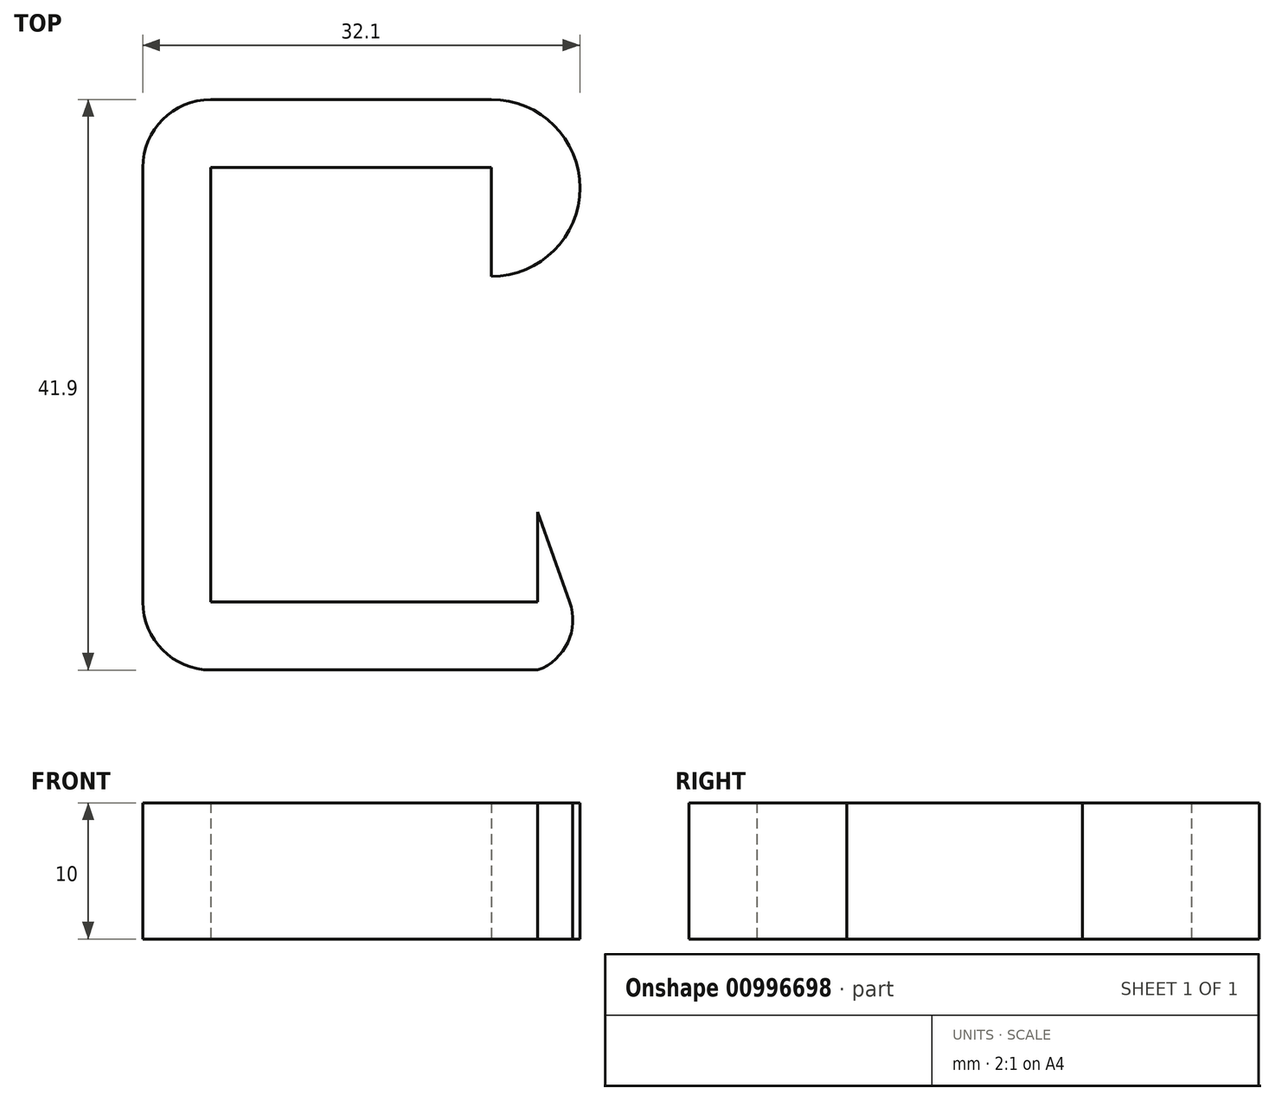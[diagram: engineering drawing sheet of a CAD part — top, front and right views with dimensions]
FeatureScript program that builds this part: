
annotation { "Feature Type Name" : "Feature", "Feature Type Description" : "" }
export const myFeature = defineFeature(function(context is Context, id is Id, definition is map)
    precondition{}
    {
        {
            var Q0;
            Q0=qCreatedBy(makeId("Top.planeOp"),FACE);
            var sketch = newSketch(context, id + "F0", { "sketchPlane" : qUnion([Q0])});
            skLineSegment(sketch, "E0", {"start": v(4.2, 20.2) * mm, "end": v(-16.4, 20.2) * mm});
            skLineSegment(sketch, "E1", {"start": v(-16.4, 20.2) * mm, "end": v(-16.4, -11.7) * mm});
            skLineSegment(sketch, "E2", {"start": v(-16.4, -11.7) * mm, "end": v(7.6, -11.7) * mm});
            skLineSegment(sketch, "E3", {"start": v(4.2, 20.2) * mm, "end": v(4.2, 12.2) * mm});
            skLineSegment(sketch, "E4.0", {"start": v(4.2, 25.2) * mm, "end": v(-16.4, 25.2) * mm});
            skLineSegment(sketch, "E5.0", {"start": v(-21.4, 20.2) * mm, "end": v(-21.4, -11.7) * mm});
            skLineSegment(sketch, "E6.0", {"start": v(-16.4, -16.7) * mm, "end": v(7.6, -16.7) * mm});
            skArc(sketch, "E7", {"start": v(-21.4, -11.7) * mm, "mid": v(-19.94, -15.24) * mm, "end": v(-16.4, -16.7) * mm});
            skArc(sketch, "E8", {"start": v(-16.4, 25.2) * mm, "mid": v(-19.94, 23.73) * mm, "end": v(-21.4, 20.2) * mm});
            skArc(sketch, "E9", {"start": v(4.2, 12.2) * mm, "mid": v(10.7, 18.7) * mm, "end": v(4.2, 25.2) * mm});
            skLineSegment(sketch, "E10", {"start": v(7.6, -11.7) * mm, "end": v(7.6, -5.1) * mm});
            skLineSegment(sketch, "E11", {"start": v(7.6, -5.1) * mm, "end": v(9.94, -11.7) * mm});
            skArc(sketch, "E12", {"start": v(7.6, -16.7) * mm, "mid": v(9.8, -14.7) * mm, "end": v(9.94, -11.7) * mm});
            skSolve(sketch);
        }
        {
            var Q0;
            Q0 = qSketchRegion(id + "F0", true);
            extrude(context, id + "F1", {"entities" : qUnion([Q0]), "depth" : 10 * mm, "offsetDistance" : 25 * mm});
        }
    });
